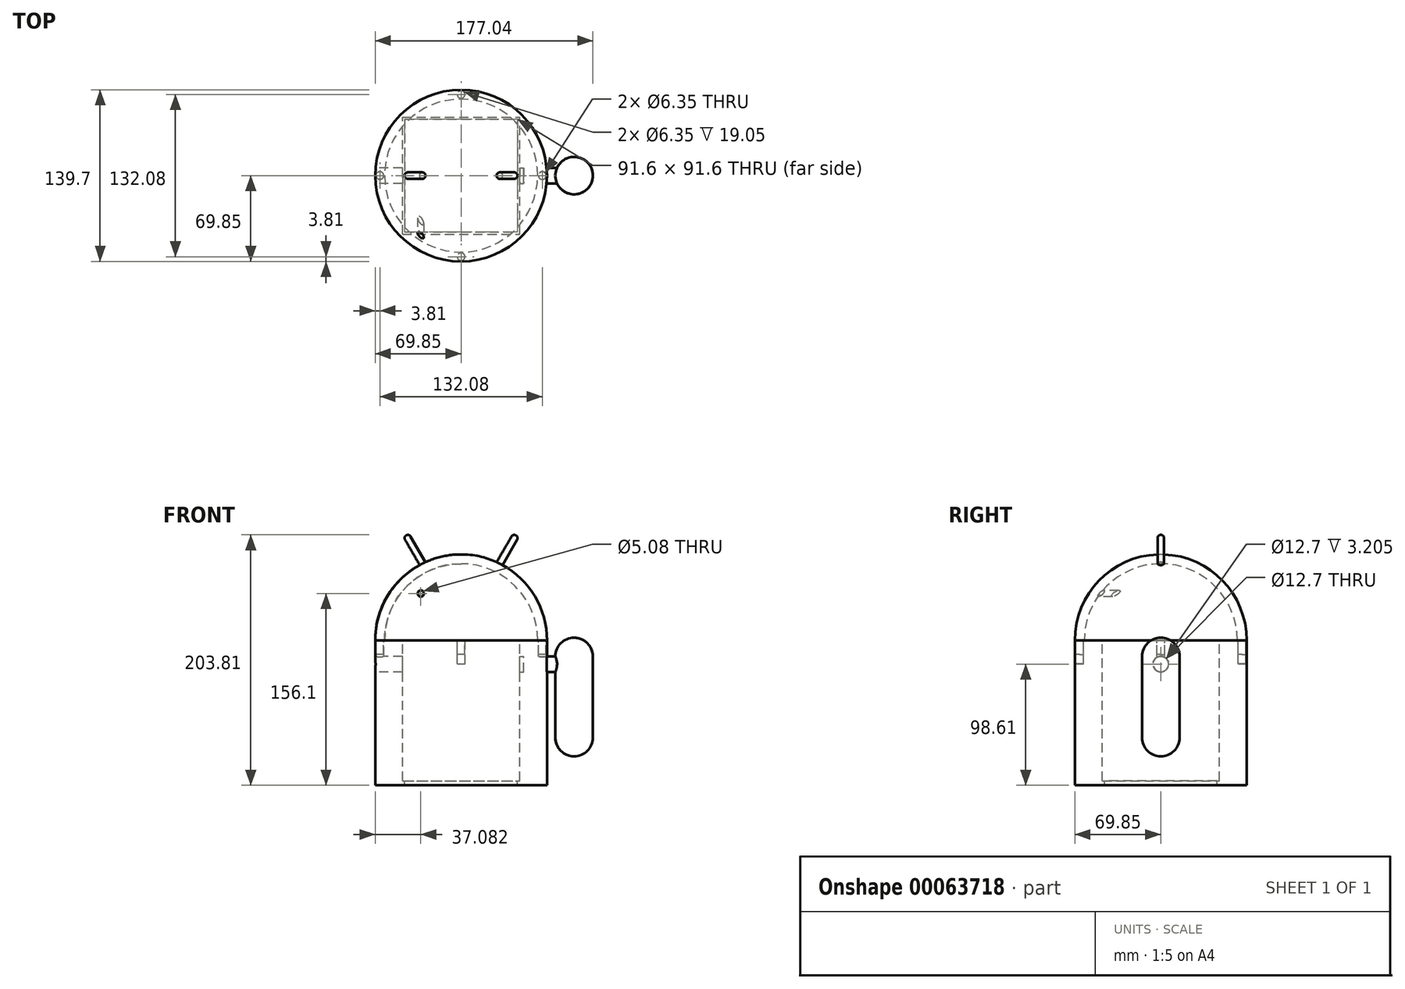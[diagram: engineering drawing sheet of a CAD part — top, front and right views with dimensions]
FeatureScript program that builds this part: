
annotation { "Feature Type Name" : "Feature", "Feature Type Description" : "" }
export const myFeature = defineFeature(function(context is Context, id is Id, definition is map)
    precondition{}
    {
        {
            var Q0;
            Q0=qCreatedBy(makeId("Front.planeOp"),FACE);
            cPlane(context, id + "F0", {"entities" : qUnion([Q0]), "cplaneType" : CPlaneType.OFFSET, "offset" : 76.2 * mm, "width" : 152.4 * mm, "height" : 152.4 * mm});
        }
        {
            var Q0;
            Q0=qCreatedBy(makeId("Front.planeOp"),FACE);
            var sketch = newSketch(context, id + "F1", { "sketchPlane" : qUnion([Q0])});
            skLineSegment(sketch, "E0.rect.bottom", {"start": v(0, 49.94) * mm, "end": v(-69.85, 49.94) * mm});
            skLineSegment(sketch, "E0.rect.right", {"start": v(-69.85, 49.94) * mm, "end": v(-69.85, -49.94) * mm});
            skPoint(sketch, "E0.rect.middle", {"position": v(0, 0) * mm});
            skLineSegment(sketch, "E1.top", {"start": v(-69.85, -68.13) * mm, "end": v(0, -68.13) * mm});
            skLineSegment(sketch, "E1.left", {"start": v(-69.85, -49.94) * mm, "end": v(-69.85, -68.13) * mm});
            skArc(sketch, "E2", {"start": v(0, 119.8) * mm, "mid": v(-49.4, 99.33) * mm, "end": v(-69.85, 49.94) * mm});
            skLineSegment(sketch, "E3", {"start": v(0, 119.8) * mm, "end": v(0, -68.13) * mm});
            skLineSegment(sketch, "E4", {"start": v(-31.34, 112.37) * mm, "end": v(-43.3, 133.06) * mm});
            skPoint(sketch, "E0.rect.left.end.orphan", {"position": v(69.85, -49.94) * mm});
            skPoint(sketch, "E5.orphan", {"position": v(69.85, 49.94) * mm});
            skPoint(sketch, "E6.orphan", {"position": v(69.85, -68.13) * mm});
            skLineSegment(sketch, "E7", {"start": v(-43.3, 133.06) * mm, "end": v(-41.04, 134.37) * mm});
            skLineSegment(sketch, "E8", {"start": v(-41.04, 134.37) * mm, "end": v(-28.97, 113.5) * mm});
            skArc(sketch, "E9", {"start": v(-41.04, 134.37) * mm, "mid": v(-42.63, 135.6) * mm, "end": v(-44.61, 135.33) * mm});
            skLineSegment(sketch, "E10", {"start": v(-43.3, 133.06) * mm, "end": v(-44.61, 135.33) * mm});
            skPoint(sketch, "E11.start.orphan", {"position": v(-45.57, 131.75) * mm});
            skLineSegment(sketch, "E12.MirrorCS", {"start": v(43.3, 133.06) * mm, "end": v(44.61, 135.33) * mm});
            skArc(sketch, "E13.MirrorCS", {"start": v(41.04, 134.37) * mm, "mid": v(42.63, 135.6) * mm, "end": v(44.61, 135.33) * mm});
            skLineSegment(sketch, "E14.MirrorCS", {"start": v(43.3, 133.06) * mm, "end": v(41.04, 134.37) * mm});
            skLineSegment(sketch, "E15.MirrorCS", {"start": v(41.04, 134.37) * mm, "end": v(28.97, 113.5) * mm});
            skLineSegment(sketch, "E16.MirrorCS", {"start": v(31.34, 112.37) * mm, "end": v(43.3, 133.06) * mm});
            skLineSegment(sketch, "E17", {"start": v(28.97, 113.5) * mm, "end": v(31.34, 112.37) * mm});
            skSolve(sketch);
        }
        {
            var Q0;
            {var subQ1=sQuery(id+"F1.wireOp",EDGE,"E0.rect.bottom");Q0=makeQuery(id+"F1.imprint","IMPRINT",FACE,{"disambiguationData":[TD([[makeQuery(id+"F1.imprint","IMPRINT",EDGE,{"derivedFrom":subQ1}),-1.0]])]});}
            var Q1;
            Q1=sQuery(id+"F1.wireOp",EDGE,"E3");
            revolve(context, id + "F2", {"entities" : qUnion([Q0]), "axis" : qUnion([Q1]), "revolveType" : RevolveType.FULL});
        }
        {
            var Q0;
            Q0=makeQuery(id+"F2.opRevolve","SWEPT_FACE",FACE,{"disambiguationData":[OSD([sQuery(id+"F1.wireOp",EDGE,"E0.rect.bottom")])]});
            var Q1;
            Q1=makeQuery(id+"F2.opRevolve","SWEPT_BODY",BODY,{"disambiguationData":[OSD([sQuery(id+"F1.wireOp",EDGE,"E0.rect.bottom"),sQuery(id+"F1.wireOp",EDGE,"E2"),sQuery(id+"F1.wireOp",EDGE,"E3")])]});
            shell(context, id + "F3", {"entities" : qUnion([Q0]), "parts" : qUnion([Q1]), "thickness" : 7.62 * mm});
        }
        {
            var Q0;
            {var subQ0=sQuery(id+"F1.wireOp",EDGE,"E4");Q0=makeQuery(id+"F1.imprint","IMPRINT",FACE,{"disambiguationData":[TD([[makeQuery(id+"F1.imprint","IMPRINT",EDGE,{"derivedFrom":subQ0}),-1.0]])]});}
            var Q1;
            Q1=makeQuery(id+"F1.imprint","IMPRINT",FACE,{"disambiguationData":[TD([[makeQuery(id+"F1.imprint","IMPRINT",EDGE,{"derivedFrom":sQuery(id+"F1.wireOp",EDGE,"E7")}),1.0]])]});
            var Q2;
            Q2=sQuery(id+"F1.wireOp",EDGE,"E4");
            revolve(context, id + "F4", {"operationType" : NewBodyOperationType.ADD, "entities" : qUnion([Q0, Q1]), "axis" : qUnion([Q2]), "revolveType" : RevolveType.FULL});
        }
        {
            var Q0;
            Q0=makeQuery(id+"F1.imprint","IMPRINT",FACE,{"disambiguationData":[TD([[makeQuery(id+"F1.imprint","IMPRINT",EDGE,{"derivedFrom":sQuery(id+"F1.wireOp",EDGE,"E14.MirrorCS")}),1.0]])]});
            var Q1;
            Q1=makeQuery(id+"F1.imprint","IMPRINT",FACE,{"disambiguationData":[TD([[makeQuery(id+"F1.imprint","IMPRINT",EDGE,{"derivedFrom":sQuery(id+"F1.wireOp",EDGE,"E12.MirrorCS")}),1.0]])]});
            var Q2;
            Q2=sQuery(id+"F1.wireOp",EDGE,"E16.MirrorCS");
            revolve(context, id + "F5", {"operationType" : NewBodyOperationType.ADD, "entities" : qUnion([Q0, Q1]), "axis" : qUnion([Q2]), "revolveType" : RevolveType.FULL});
        }
        {
            var Q0;
            {var subQ2=sQuery(id+"F1.wireOp",EDGE,"E0.rect.bottom");Q0=makeQuery(id+"F1.imprint","IMPRINT",FACE,{"disambiguationData":[TD([[makeQuery(id+"F1.imprint","IMPRINT",EDGE,{"derivedFrom":subQ2}),1.0]])]});}
            var Q1;
            Q1=sQuery(id+"F1.wireOp",EDGE,"E3");
            revolve(context, id + "F6", {"entities" : qUnion([Q0]), "axis" : qUnion([Q1]), "revolveType" : RevolveType.FULL});
        }
        {
            var Q0;
            Q0=qCreatedBy(id+"F0.planeOp",FACE);
            var sketch = newSketch(context, id + "F7", { "sketchPlane" : qUnion([Q0])});
            skCircle(sketch, "E18", {"center": v(-32.77, 87.97) * mm, "radius": 2.54 * mm});
            skCircle(sketch, "E19.MirrorC", {"center": v(32.77, 87.97) * mm, "radius": 2.54 * mm});
            skSolve(sketch);
        }
        {
            var Q0;
            Q0=makeQuery(id+"F7.imprint","IMPRINT",FACE,{"disambiguationData":[TD([[makeQuery(id+"F7.imprint","IMPRINT",EDGE,{"derivedFrom":sQuery(id+"F7.wireOp",EDGE,"E18")}),1.0]])]});
            var Q1;
            Q1=makeQuery(id+"F7.imprint","IMPRINT",FACE,{"disambiguationData":[TD([[makeQuery(id+"F7.imprint","IMPRINT",EDGE,{"derivedFrom":sQuery(id+"F7.wireOp",EDGE,"E19.MirrorC")}),-1.0]])]});
            var Q2;
            Q2=makeQuery(id+"F7.imprint","IMPRINT",FACE,{"disambiguationData":[TD([[makeQuery(id+"F7.imprint","IMPRINT",EDGE,{"derivedFrom":sQuery(id+"F7.wireOp",EDGE,"E19.MirrorC")}),-1.0]])]});
            var Q3;
            Q3=sQuery(id+"F7.wireOp",EDGE,"E18");
            var Q4;
            Q4=sQuery(id+"F7.wireOp",EDGE,"3ee3cfb3-d9ed-4d06-a01c-7e7985c390ca0.MirrorC");
            extrude(context, id + "F8", {"entities" : qUnion([Q0, Q1, Q2]), "operationType" : NewBodyOperationType.REMOVE, "surfaceEntities" : qUnion([Q3, Q4]), "oppositeDirection" : true, "depth" : 50.8 * mm});
        }
        {
            var Q0;
            Q0=makeQuery(id+"F6.opRevolve","SWEPT_FACE",FACE,{"disambiguationData":[OSD([sQuery(id+"F1.wireOp",EDGE,"E0.rect.bottom")])]});
            var sketch = newSketch(context, id + "F9", { "sketchPlane" : qUnion([Q0])});
            skPoint(sketch, "E20", {"position": v(49.4, 49.4) * mm});
            skPoint(sketch, "E21", {"position": v(-49.4, -49.4) * mm});
            skLineSegment(sketch, "E22.bottom", {"start": v(-49.4, -49.4) * mm, "end": v(49.4, -49.4) * mm});
            skLineSegment(sketch, "E22.top", {"start": v(-49.4, 49.4) * mm, "end": v(49.4, 49.4) * mm});
            skLineSegment(sketch, "E22.left", {"start": v(-49.4, -49.4) * mm, "end": v(-49.4, 49.4) * mm});
            skLineSegment(sketch, "E22.right", {"start": v(49.4, -49.4) * mm, "end": v(49.4, 49.4) * mm});
            skPoint(sketch, "E23", {"position": v(-47.6, -47.6) * mm});
            skPoint(sketch, "E24", {"position": v(47.6, 47.6) * mm});
            skLineSegment(sketch, "E25.bottom", {"start": v(-47.6, -47.6) * mm, "end": v(47.6, -47.6) * mm});
            skLineSegment(sketch, "E25.top", {"start": v(-47.6, 47.6) * mm, "end": v(47.6, 47.6) * mm});
            skLineSegment(sketch, "E25.left", {"start": v(-47.6, -47.6) * mm, "end": v(-47.6, 47.6) * mm});
            skLineSegment(sketch, "E25.right", {"start": v(47.6, -47.6) * mm, "end": v(47.6, 47.6) * mm});
            skLineSegment(sketch, "E26", {"start": v(-47.6, 47.6) * mm, "end": v(47.6, -47.6) * mm});
            skLineSegment(sketch, "E27.bottom", {"start": v(-45.8, 45.8) * mm, "end": v(45.8, 45.8) * mm});
            skLineSegment(sketch, "E27.top", {"start": v(-45.8, -45.8) * mm, "end": v(45.8, -45.8) * mm});
            skLineSegment(sketch, "E27.left", {"start": v(-45.8, 45.8) * mm, "end": v(-45.8, -45.8) * mm});
            skLineSegment(sketch, "E27.right", {"start": v(45.8, 45.8) * mm, "end": v(45.8, -45.8) * mm});
            skSolve(sketch);
        }
        {
            var Q0;
            {var subQ0=sQuery(id+"F9.wireOp",EDGE,"E27.bottom");Q0=makeQuery(id+"F9.imprint","IMPRINT",FACE,{"disambiguationData":[TD([[makeQuery(id+"F9.imprint","IMPRINT",EDGE,{"derivedFrom":subQ0}),-1.0]])]});}
            var Q1;
            {var subQ2=sQuery(id+"F9.wireOp",EDGE,"E27.top");Q1=makeQuery(id+"F9.imprint","IMPRINT",FACE,{"disambiguationData":[TD([[makeQuery(id+"F9.imprint","IMPRINT",EDGE,{"derivedFrom":subQ2}),1.0]])]});}
            extrude(context, id + "F10", {"entities" : qUnion([Q0, Q1]), "operationType" : NewBodyOperationType.REMOVE, "oppositeDirection" : true, "depth" : 152.4 * mm});
        }
        {
            var Q0;
            {var subQ3=sQuery(id+"F9.wireOp",EDGE,"E25.top");Q0=makeQuery(id+"F9.imprint","IMPRINT",FACE,{"disambiguationData":[TD([[makeQuery(id+"F9.imprint","IMPRINT",EDGE,{"derivedFrom":subQ3}),-1.0]])]});}
            var Q1;
            {var subQ1=sQuery(id+"F9.wireOp",EDGE,"E25.bottom");Q1=makeQuery(id+"F9.imprint","IMPRINT",FACE,{"disambiguationData":[TD([[makeQuery(id+"F9.imprint","IMPRINT",EDGE,{"derivedFrom":subQ1}),1.0]])]});}
            extrude(context, id + "F11", {"entities" : qUnion([Q0, Q1]), "operationType" : NewBodyOperationType.REMOVE, "oppositeDirection" : true, "depth" : 114.3 * mm});
        }
        {
            var Q0;
            Q0=makeQuery(id+"F2.opRevolve","SWEPT_FACE",FACE,{"disambiguationData":[OSD([sQuery(id+"F1.wireOp",EDGE,"E0.rect.bottom")])]});
            var sketch = newSketch(context, id + "F12", { "sketchPlane" : qUnion([Q0])});
            skLineSegment(sketch, "E28", {"start": v(62.23, 0) * mm, "end": v(69.85, 0) * mm});
            skLineSegment(sketch, "E29", {"start": v(0, 62.23) * mm, "end": v(0, 69.85) * mm});
            skLineSegment(sketch, "E30", {"start": v(-62.23, 0) * mm, "end": v(-69.85, 0) * mm});
            skLineSegment(sketch, "E31", {"start": v(0, -62.23) * mm, "end": v(0, -69.85) * mm});
            skCircle(sketch, "E32", {"center": v(0, 66.04) * mm, "radius": 3.18 * mm});
            skCircle(sketch, "E33", {"center": v(66.04, 0) * mm, "radius": 3.18 * mm});
            skCircle(sketch, "E34", {"center": v(0, -66.04) * mm, "radius": 3.18 * mm});
            skCircle(sketch, "E35", {"center": v(-66.04, 0) * mm, "radius": 3.18 * mm});
            skSolve(sketch);
        }
        {
            var Q0;
            {var subQ0=sQuery(id+"F12.wireOp",EDGE,"E35");var subQ1=sQuery(id+"F12.wireOp",EDGE,"E30");var subQ2=makeQuery(id+"F12.imprint","INTERSECT",VERTEX,{"disambiguationData":[OD(0.0)],"derivedFrom":[subQ1,subQ0]});Q0=makeQuery(id+"F12.imprint","IMPRINT",FACE,{"disambiguationData":[TD([[makeQuery(id+"F12.imprint","IMPRINT",EDGE,{"disambiguationData":[TD([[subQ2,-1.0]])],"derivedFrom":subQ1}),1.0]])]});}
            var Q1;
            {var subQ0=sQuery(id+"F12.wireOp",EDGE,"E35");var subQ1=sQuery(id+"F12.wireOp",EDGE,"E30");var subQ2=makeQuery(id+"F12.imprint","INTERSECT",VERTEX,{"disambiguationData":[OD(0.0)],"derivedFrom":[subQ1,subQ0]});Q1=makeQuery(id+"F12.imprint","IMPRINT",FACE,{"disambiguationData":[TD([[makeQuery(id+"F12.imprint","IMPRINT",EDGE,{"disambiguationData":[TD([[subQ2,-1.0]])],"derivedFrom":subQ1}),-1.0]])]});}
            var Q2;
            {var subQ0=sQuery(id+"F12.wireOp",EDGE,"E32");var subQ1=sQuery(id+"F12.wireOp",EDGE,"E29");var subQ2=makeQuery(id+"F12.imprint","INTERSECT",VERTEX,{"disambiguationData":[OD(0.0)],"derivedFrom":[subQ1,subQ0]});Q2=makeQuery(id+"F12.imprint","IMPRINT",FACE,{"disambiguationData":[TD([[makeQuery(id+"F12.imprint","IMPRINT",EDGE,{"disambiguationData":[TD([[subQ2,-1.0]])],"derivedFrom":subQ1}),-1.0]])]});}
            var Q3;
            {var subQ0=sQuery(id+"F12.wireOp",EDGE,"E32");var subQ1=sQuery(id+"F12.wireOp",EDGE,"E29");var subQ2=makeQuery(id+"F12.imprint","INTERSECT",VERTEX,{"disambiguationData":[OD(0.0)],"derivedFrom":[subQ1,subQ0]});Q3=makeQuery(id+"F12.imprint","IMPRINT",FACE,{"disambiguationData":[TD([[makeQuery(id+"F12.imprint","IMPRINT",EDGE,{"disambiguationData":[TD([[subQ2,-1.0]])],"derivedFrom":subQ1}),1.0]])]});}
            var Q4;
            {var subQ0=sQuery(id+"F12.wireOp",EDGE,"E33");var subQ1=sQuery(id+"F12.wireOp",EDGE,"E28");var subQ2=makeQuery(id+"F12.imprint","INTERSECT",VERTEX,{"disambiguationData":[OD(0.0)],"derivedFrom":[subQ1,subQ0]});Q4=makeQuery(id+"F12.imprint","IMPRINT",FACE,{"disambiguationData":[TD([[makeQuery(id+"F12.imprint","IMPRINT",EDGE,{"disambiguationData":[TD([[subQ2,-1.0]])],"derivedFrom":subQ1}),1.0]])]});}
            var Q5;
            {var subQ0=sQuery(id+"F12.wireOp",EDGE,"E33");var subQ1=sQuery(id+"F12.wireOp",EDGE,"E28");var subQ2=makeQuery(id+"F12.imprint","INTERSECT",VERTEX,{"disambiguationData":[OD(0.0)],"derivedFrom":[subQ1,subQ0]});Q5=makeQuery(id+"F12.imprint","IMPRINT",FACE,{"disambiguationData":[TD([[makeQuery(id+"F12.imprint","IMPRINT",EDGE,{"disambiguationData":[TD([[subQ2,-1.0]])],"derivedFrom":subQ1}),-1.0]])]});}
            var Q6;
            {var subQ0=sQuery(id+"F12.wireOp",EDGE,"E34");var subQ1=sQuery(id+"F12.wireOp",EDGE,"E31");var subQ2=makeQuery(id+"F12.imprint","INTERSECT",VERTEX,{"disambiguationData":[OD(0.0)],"derivedFrom":[subQ1,subQ0]});Q6=makeQuery(id+"F12.imprint","IMPRINT",FACE,{"disambiguationData":[TD([[makeQuery(id+"F12.imprint","IMPRINT",EDGE,{"disambiguationData":[TD([[subQ2,-1.0]])],"derivedFrom":subQ1}),1.0]])]});}
            var Q7;
            {var subQ0=sQuery(id+"F12.wireOp",EDGE,"E34");var subQ1=sQuery(id+"F12.wireOp",EDGE,"E31");var subQ2=makeQuery(id+"F12.imprint","INTERSECT",VERTEX,{"disambiguationData":[OD(0.0)],"derivedFrom":[subQ1,subQ0]});Q7=makeQuery(id+"F12.imprint","IMPRINT",FACE,{"disambiguationData":[TD([[makeQuery(id+"F12.imprint","IMPRINT",EDGE,{"disambiguationData":[TD([[subQ2,-1.0]])],"derivedFrom":subQ1}),-1.0]])]});}
            extrude(context, id + "F13", {"entities" : qUnion([Q0, Q1, Q2, Q3, Q4, Q5, Q6, Q7]), "operationType" : NewBodyOperationType.REMOVE, "depth" : 19.05 * mm});
        }
        {
            var Q0;
            Q0=makeQuery(id+"F2.opRevolve","SWEPT_FACE",FACE,{"disambiguationData":[OSD([sQuery(id+"F1.wireOp",EDGE,"E0.rect.bottom")])]});
            var sketch = newSketch(context, id + "F14", { "sketchPlane" : qUnion([Q0])});
            skLineSegment(sketch, "E36", {"start": v(0, 62.23) * mm, "end": v(0, 69.85) * mm});
            skLineSegment(sketch, "E37", {"start": v(62.23, 0) * mm, "end": v(69.85, 0) * mm});
            skLineSegment(sketch, "E38", {"start": v(0, -62.23) * mm, "end": v(0, -69.85) * mm});
            skLineSegment(sketch, "E39", {"start": v(-62.23, 0) * mm, "end": v(-69.85, 0) * mm});
            skCircle(sketch, "E40", {"center": v(66.04, 0) * mm, "radius": 3.11 * mm});
            skCircle(sketch, "E41", {"center": v(0, -66.04) * mm, "radius": 3.11 * mm});
            skCircle(sketch, "E42", {"center": v(-66.04, 0) * mm, "radius": 3.11 * mm});
            skCircle(sketch, "E43", {"center": v(0, 66.04) * mm, "radius": 3.11 * mm});
            skSolve(sketch);
        }
        {
            var Q0;
            {var subQ0=sQuery(id+"F14.wireOp",EDGE,"E43");var subQ1=sQuery(id+"F14.wireOp",EDGE,"E36");var subQ2=makeQuery(id+"F14.imprint","INTERSECT",VERTEX,{"disambiguationData":[OD(0.0)],"derivedFrom":[subQ1,subQ0]});Q0=makeQuery(id+"F14.imprint","IMPRINT",FACE,{"disambiguationData":[TD([[makeQuery(id+"F14.imprint","IMPRINT",EDGE,{"disambiguationData":[TD([[subQ2,-1.0]])],"derivedFrom":subQ1}),1.0]])]});}
            var Q1;
            {var subQ0=sQuery(id+"F14.wireOp",EDGE,"E43");var subQ1=sQuery(id+"F14.wireOp",EDGE,"E36");var subQ2=makeQuery(id+"F14.imprint","INTERSECT",VERTEX,{"disambiguationData":[OD(0.0)],"derivedFrom":[subQ1,subQ0]});Q1=makeQuery(id+"F14.imprint","IMPRINT",FACE,{"disambiguationData":[TD([[makeQuery(id+"F14.imprint","IMPRINT",EDGE,{"disambiguationData":[TD([[subQ2,-1.0]])],"derivedFrom":subQ1}),-1.0]])]});}
            var Q2;
            {var subQ0=sQuery(id+"F14.wireOp",EDGE,"E42");var subQ1=sQuery(id+"F14.wireOp",EDGE,"E39");var subQ2=makeQuery(id+"F14.imprint","INTERSECT",VERTEX,{"disambiguationData":[OD(0.0)],"derivedFrom":[subQ1,subQ0]});Q2=makeQuery(id+"F14.imprint","IMPRINT",FACE,{"disambiguationData":[TD([[makeQuery(id+"F14.imprint","IMPRINT",EDGE,{"disambiguationData":[TD([[subQ2,-1.0]])],"derivedFrom":subQ1}),-1.0]])]});}
            var Q3;
            {var subQ0=sQuery(id+"F14.wireOp",EDGE,"E42");var subQ1=sQuery(id+"F14.wireOp",EDGE,"E39");var subQ2=makeQuery(id+"F14.imprint","INTERSECT",VERTEX,{"disambiguationData":[OD(0.0)],"derivedFrom":[subQ1,subQ0]});Q3=makeQuery(id+"F14.imprint","IMPRINT",FACE,{"disambiguationData":[TD([[makeQuery(id+"F14.imprint","IMPRINT",EDGE,{"disambiguationData":[TD([[subQ2,-1.0]])],"derivedFrom":subQ1}),1.0]])]});}
            var Q4;
            {var subQ0=sQuery(id+"F14.wireOp",EDGE,"E41");var subQ1=sQuery(id+"F14.wireOp",EDGE,"E38");var subQ2=makeQuery(id+"F14.imprint","INTERSECT",VERTEX,{"disambiguationData":[OD(0.0)],"derivedFrom":[subQ1,subQ0]});Q4=makeQuery(id+"F14.imprint","IMPRINT",FACE,{"disambiguationData":[TD([[makeQuery(id+"F14.imprint","IMPRINT",EDGE,{"disambiguationData":[TD([[subQ2,-1.0]])],"derivedFrom":subQ1}),1.0]])]});}
            var Q5;
            {var subQ0=sQuery(id+"F14.wireOp",EDGE,"E41");var subQ1=sQuery(id+"F14.wireOp",EDGE,"E38");var subQ2=makeQuery(id+"F14.imprint","INTERSECT",VERTEX,{"disambiguationData":[OD(0.0)],"derivedFrom":[subQ1,subQ0]});Q5=makeQuery(id+"F14.imprint","IMPRINT",FACE,{"disambiguationData":[TD([[makeQuery(id+"F14.imprint","IMPRINT",EDGE,{"disambiguationData":[TD([[subQ2,-1.0]])],"derivedFrom":subQ1}),-1.0]])]});}
            var Q6;
            {var subQ0=sQuery(id+"F14.wireOp",EDGE,"E40");var subQ1=sQuery(id+"F14.wireOp",EDGE,"E37");var subQ2=makeQuery(id+"F14.imprint","INTERSECT",VERTEX,{"disambiguationData":[OD(0.0)],"derivedFrom":[subQ1,subQ0]});Q6=makeQuery(id+"F14.imprint","IMPRINT",FACE,{"disambiguationData":[TD([[makeQuery(id+"F14.imprint","IMPRINT",EDGE,{"disambiguationData":[TD([[subQ2,-1.0]])],"derivedFrom":subQ1}),1.0]])]});}
            var Q7;
            {var subQ0=sQuery(id+"F14.wireOp",EDGE,"E40");var subQ1=sQuery(id+"F14.wireOp",EDGE,"E37");var subQ2=makeQuery(id+"F14.imprint","INTERSECT",VERTEX,{"disambiguationData":[OD(0.0)],"derivedFrom":[subQ1,subQ0]});Q7=makeQuery(id+"F14.imprint","IMPRINT",FACE,{"disambiguationData":[TD([[makeQuery(id+"F14.imprint","IMPRINT",EDGE,{"disambiguationData":[TD([[subQ2,-1.0]])],"derivedFrom":subQ1}),-1.0]])]});}
            extrude(context, id + "F15", {"entities" : qUnion([Q0, Q1, Q2, Q3, Q4, Q5, Q6, Q7]), "operationType" : NewBodyOperationType.ADD, "depth" : 11.43 * mm});
        }
        {
            var Q0;
            Q0=qCreatedBy(makeId("Front.planeOp"),FACE);
            var sketch = newSketch(context, id + "F16", { "sketchPlane" : qUnion([Q0])});
            skLineSegment(sketch, "E44", {"start": v(76.7, 36.74) * mm, "end": v(76.7, -29.3) * mm});
            skArc(sketch, "E45", {"start": v(91.95, 51.98) * mm, "mid": v(81.17, 47.52) * mm, "end": v(76.7, 36.74) * mm});
            skArc(sketch, "E46", {"start": v(76.7, -29.3) * mm, "mid": v(81.17, -40.08) * mm, "end": v(91.95, -44.54) * mm});
            skLineSegment(sketch, "E47", {"start": v(91.95, 51.98) * mm, "end": v(91.95, -44.54) * mm});
            skPoint(sketch, "E48.start.orphan", {"position": v(107.19, 36.74) * mm});
            skPoint(sketch, "E49.orphan", {"position": v(107.19, -29.3) * mm});
            skSolve(sketch);
        }
        {
            var Q0;
            Q0=makeQuery(id+"F16.imprint","IMPRINT",FACE,{"disambiguationData":[TD([[makeQuery(id+"F16.imprint","IMPRINT",EDGE,{"derivedFrom":sQuery(id+"F16.wireOp",EDGE,"E44")}),1.0]])]});
            var Q1;
            Q1=sQuery(id+"F16.wireOp",EDGE,"E47");
            revolve(context, id + "F17", {"entities" : qUnion([Q0]), "axis" : qUnion([Q1]), "revolveType" : RevolveType.FULL});
        }
        {
            var Q0;
            Q0=qCreatedBy(makeId("Right.planeOp"),FACE);
            cPlane(context, id + "F18", {"entities" : qUnion([Q0]), "cplaneType" : CPlaneType.OFFSET, "offset" : 76.2 * mm, "width" : 152.4 * mm, "height" : 152.4 * mm});
        }
        {
            var Q0;
            Q0=qCreatedBy(makeId("Right.planeOp"),FACE);
            cPlane(context, id + "F19", {"entities" : qUnion([Q0]), "cplaneType" : CPlaneType.OFFSET, "offset" : 76.2 * mm, "oppositeDirection" : true, "width" : 152.4 * mm, "height" : 152.4 * mm});
        }
        {
            var Q0;
            Q0=qCreatedBy(id+"F18.planeOp",FACE);
            var sketch = newSketch(context, id + "F20", { "sketchPlane" : qUnion([Q0])});
            skLineSegment(sketch, "E50", {"start": v(0, 0) * mm, "end": v(0, 30.48) * mm});
            skCircle(sketch, "E51", {"center": v(0, 30.48) * mm, "radius": 6.35 * mm});
            skSolve(sketch);
        }
        {
            var Q0;
            Q0=makeQuery(id+"F20.imprint","IMPRINT",FACE,{"disambiguationData":[TD([[makeQuery(id+"F20.imprint","IMPRINT",EDGE,{"derivedFrom":sQuery(id+"F20.wireOp",EDGE,"E51")}),1.0]])]});
            extrude(context, id + "F21", {"entities" : qUnion([Q0]), "operationType" : NewBodyOperationType.REMOVE, "oppositeDirection" : true, "depth" : 76.2 * mm});
        }
        {
            var Q0;
            Q0=qCreatedBy(id+"F19.planeOp",FACE);
            var sketch = newSketch(context, id + "F22", { "sketchPlane" : qUnion([Q0])});
            skLineSegment(sketch, "E52", {"start": v(0, 0) * mm, "end": v(0, 30.48) * mm});
            skCircle(sketch, "E53", {"center": v(0, 30.48) * mm, "radius": 6.35 * mm});
            skSolve(sketch);
        }
        {
            var Q0;
            Q0=makeQuery(id+"F22.imprint","IMPRINT",FACE,{"disambiguationData":[TD([[makeQuery(id+"F22.imprint","IMPRINT",EDGE,{"derivedFrom":sQuery(id+"F22.wireOp",EDGE,"E53")}),1.0]])]});
            extrude(context, id + "F23", {"entities" : qUnion([Q0]), "operationType" : NewBodyOperationType.REMOVE, "depth" : 76.2 * mm});
        }
        {
            var Q0;
            Q0=qCreatedBy(makeId("Right.planeOp"),FACE);
            cPlane(context, id + "F24", {"entities" : qUnion([Q0]), "cplaneType" : CPlaneType.OFFSET, "offset" : 88.9 * mm, "width" : 152.4 * mm, "height" : 152.4 * mm});
        }
        {
            var Q0;
            Q0=qCreatedBy(id+"F24.planeOp",FACE);
            var sketch = newSketch(context, id + "F25", { "sketchPlane" : qUnion([Q0])});
            skLineSegment(sketch, "E54", {"start": v(0, 0) * mm, "end": v(0, 30.48) * mm});
            skCircle(sketch, "E55", {"center": v(0, 30.48) * mm, "radius": 6.35 * mm});
            skSolve(sketch);
        }
        {
            var Q0;
            Q0 = qSketchRegion(id + "F25", true);
            var Q1;
            Q1=sQuery(id+"F25.wireOp",EDGE,"E55");
            extrude(context, id + "F26", {"entities" : qUnion([Q0]), "operationType" : NewBodyOperationType.ADD, "surfaceEntities" : qUnion([Q1]), "oppositeDirection" : true, "depth" : 38.1 * mm});
        }
    });
